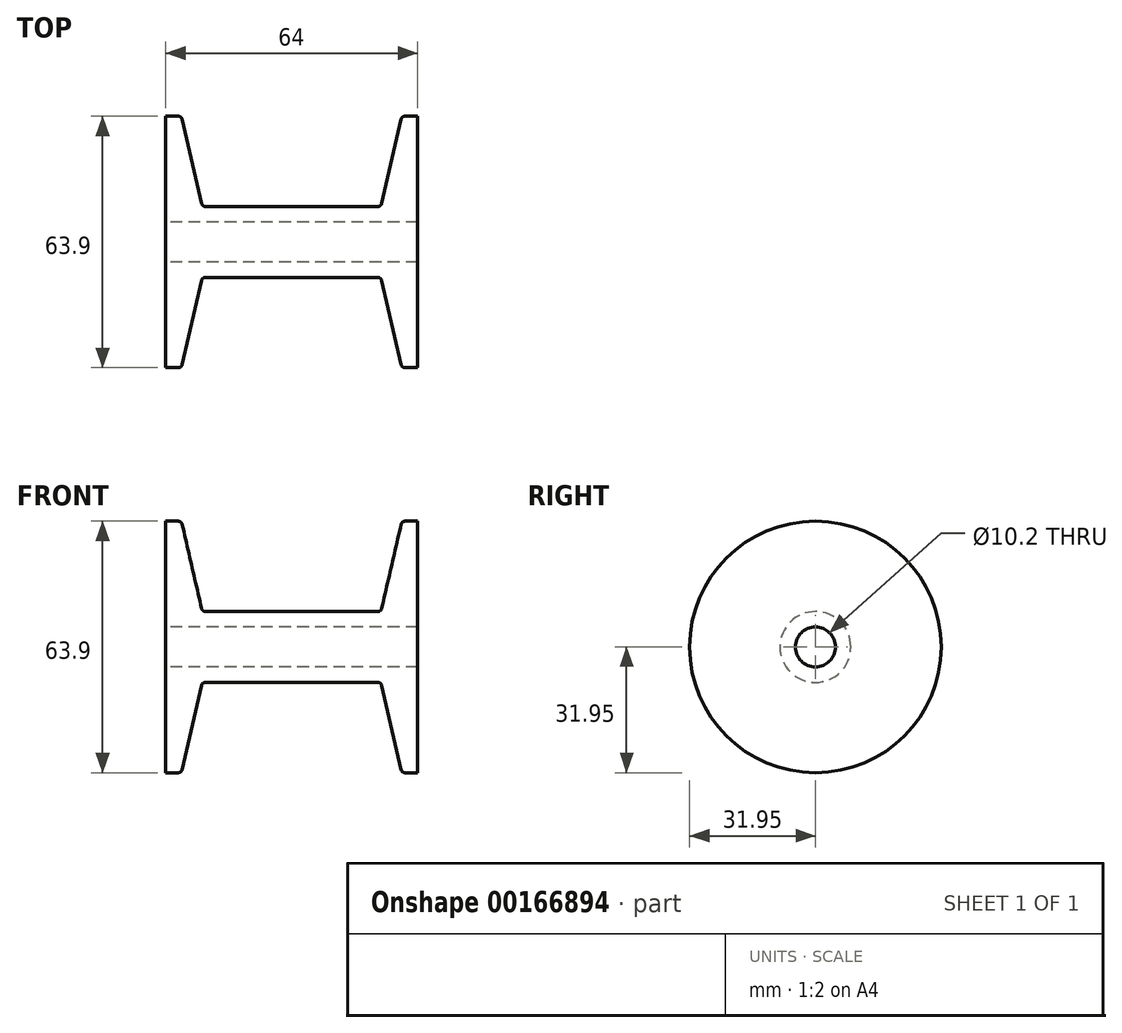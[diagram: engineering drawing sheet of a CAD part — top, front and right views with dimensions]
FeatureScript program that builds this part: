
annotation { "Feature Type Name" : "Feature", "Feature Type Description" : "" }
export const myFeature = defineFeature(function(context is Context, id is Id, definition is map)
    precondition{}
    {
        {
            var Q0;
            Q0=qCreatedBy(makeId("Front.planeOp"),FACE);
            var sketch = newSketch(context, id + "F0", { "sketchPlane" : qUnion([Q0])});
            skLineSegment(sketch, "E0", {"start": v(0, 0) * mm, "end": v(32, 0) * mm, "construction": true});
            skLineSegment(sketch, "E1", {"start": v(32, 5.1) * mm, "end": v(0, 5.1) * mm});
            skLineSegment(sketch, "E2", {"start": v(32, 5.1) * mm, "end": v(32, 31.95) * mm});
            skLineSegment(sketch, "E3", {"start": v(32, 31.95) * mm, "end": v(28.8, 31.95) * mm});
            skLineSegment(sketch, "E4", {"start": v(27.82, 31.17) * mm, "end": v(22.88, 9.78) * mm});
            skLineSegment(sketch, "E5", {"start": v(21.9, 9) * mm, "end": v(0, 9) * mm});
            skLineSegment(sketch, "E6", {"start": v(0, 0) * mm, "end": v(0, 29.08) * mm, "construction": true});
            skPoint(sketch, "E7.visualSharp", {"position": v(22.7, 9) * mm});
            skArc(sketch, "E7.filletArc", {"start": v(21.9, 9) * mm, "mid": v(22.53, 9.22) * mm, "end": v(22.88, 9.78) * mm});
            skPoint(sketch, "E8.visualSharp", {"position": v(28, 31.95) * mm});
            skArc(sketch, "E8.filletArc", {"start": v(28.8, 31.95) * mm, "mid": v(28.17, 31.73) * mm, "end": v(27.82, 31.17) * mm});
            skArc(sketch, "E9.MirrorCS", {"start": v(-28.8, 31.95) * mm, "mid": v(-28.17, 31.73) * mm, "end": v(-27.82, 31.17) * mm});
            skArc(sketch, "E10.MirrorCS", {"start": v(-21.9, 9) * mm, "mid": v(-22.53, 9.22) * mm, "end": v(-22.88, 9.78) * mm});
            skLineSegment(sketch, "E11.MirrorCS", {"start": v(-32, 31.95) * mm, "end": v(-28.8, 31.95) * mm});
            skPoint(sketch, "E12.MirrorP", {"position": v(-22.7, 9) * mm});
            skLineSegment(sketch, "E13.MirrorCS", {"start": v(-32, 5.1) * mm, "end": v(0, 5.1) * mm});
            skLineSegment(sketch, "E14.MirrorCS", {"start": v(-21.9, 9) * mm, "end": v(0, 9) * mm});
            skLineSegment(sketch, "E15.MirrorCS", {"start": v(-27.82, 31.17) * mm, "end": v(-22.88, 9.78) * mm});
            skLineSegment(sketch, "E16.MirrorCS", {"start": v(-32, 5.1) * mm, "end": v(-32, 31.95) * mm});
            skPoint(sketch, "E17.MirrorP", {"position": v(-28, 31.95) * mm});
            skSolve(sketch);
        }
        {
            var Q0;
            Q0 = qSketchRegion(id + "F0", true);
            var Q1;
            Q1=sQuery(id+"F0.wireOp",EDGE,"E0");
            revolve(context, id + "F1", {"entities" : qUnion([Q0]), "axis" : qUnion([Q1]), "revolveType" : RevolveType.FULL});
        }
    });
